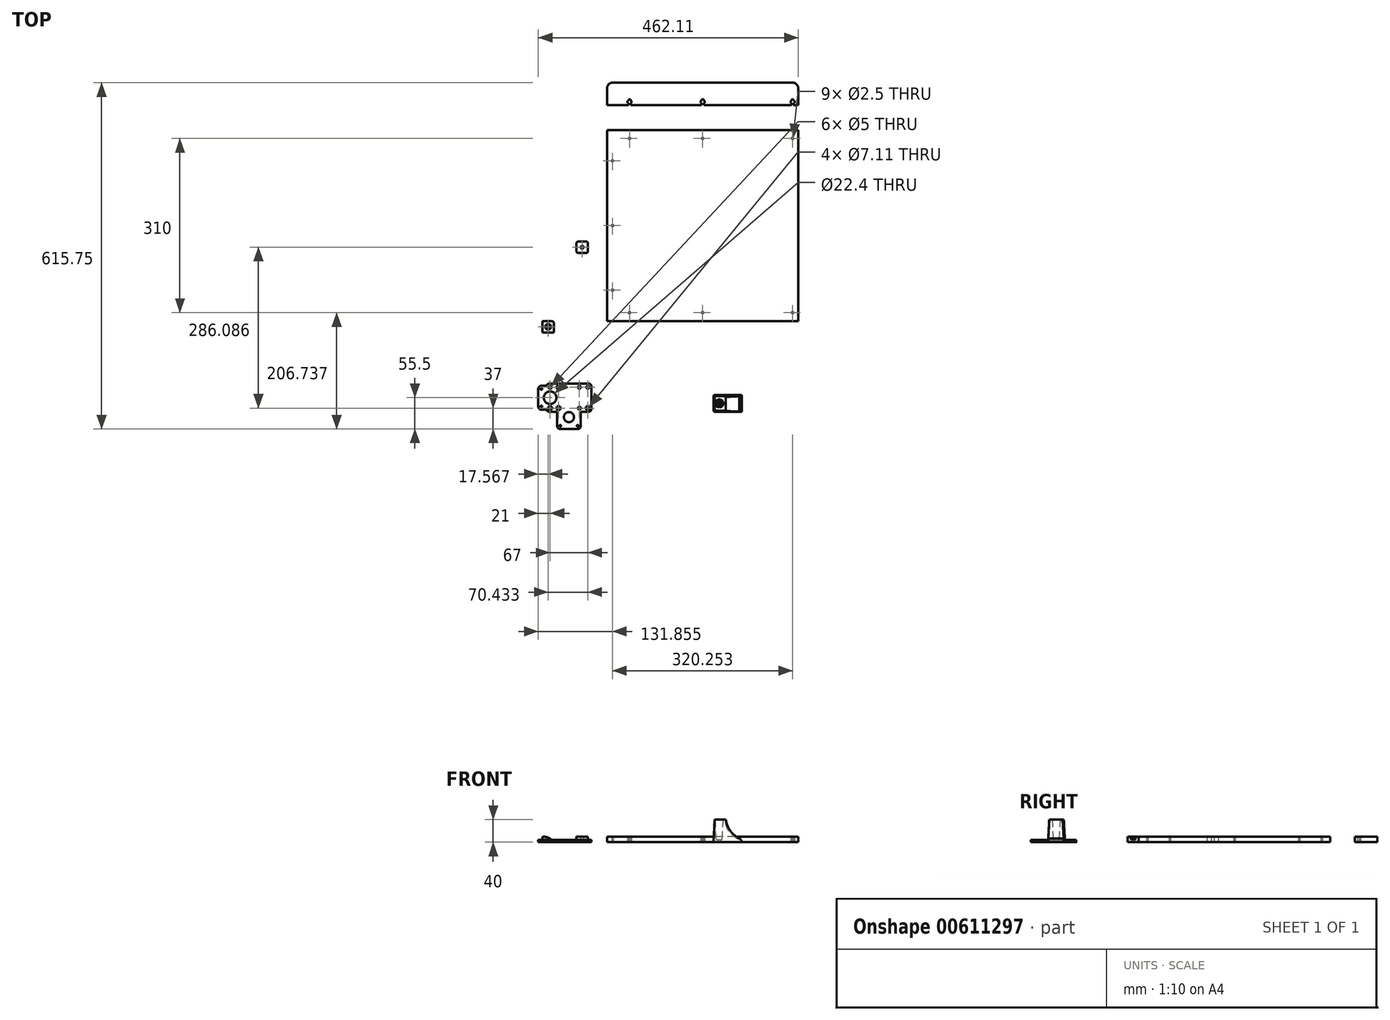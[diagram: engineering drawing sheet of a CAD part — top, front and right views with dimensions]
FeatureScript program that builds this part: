
annotation { "Feature Type Name" : "Feature", "Feature Type Description" : "" }
export const myFeature = defineFeature(function(context is Context, id is Id, definition is map)
    precondition{}
    {
        {
            var Q0;
            Q0=qCreatedBy(makeId("Top.planeOp"),FACE);
            var sketch = newSketch(context, id + "F0", { "sketchPlane" : qUnion([Q0])});
            skLineSegment(sketch, "E0.left", {"start": v(-18.5, 18.5) * mm, "end": v(-18.5, -18.5) * mm, "construction": true});
            skLineSegment(sketch, "E0.right", {"start": v(18.5, 18.5) * mm, "end": v(18.5, -18.5) * mm, "construction": true});
            skCircle(sketch, "E1", {"center": v(-18.5, 18.5) * mm, "radius": 3.56 * mm});
            skCircle(sketch, "E2", {"center": v(18.5, 18.5) * mm, "radius": 2.5 * mm});
            skCircle(sketch, "E3", {"center": v(18.5, -18.5) * mm, "radius": 2.5 * mm});
            skCircle(sketch, "E4", {"center": v(-18.5, -18.5) * mm, "radius": 3.56 * mm});
            skLineSegment(sketch, "E5.bottom", {"start": v(-35, 25) * mm, "end": v(35, 25) * mm});
            skLineSegment(sketch, "E5.top", {"start": v(-35, -25) * mm, "end": v(0.1, -25) * mm});
            skLineSegment(sketch, "E5.right", {"start": v(40, 20) * mm, "end": v(40, -20) * mm});
            skPoint(sketch, "E6.visualSharp", {"position": v(-40, 25) * mm});
            skArc(sketch, "E6.filletArc", {"start": v(-35, 25) * mm, "mid": v(-38.54, 23.54) * mm, "end": v(-40, 20) * mm});
            skPoint(sketch, "E7.visualSharp", {"position": v(40, 25) * mm});
            skArc(sketch, "E7.filletArc", {"start": v(40, 20) * mm, "mid": v(38.54, 23.54) * mm, "end": v(35, 25) * mm});
            skPoint(sketch, "E8.visualSharp", {"position": v(40, -25) * mm});
            skArc(sketch, "E8.filletArc", {"start": v(35, -25) * mm, "mid": v(38.54, -23.54) * mm, "end": v(40, -20) * mm});
            skPoint(sketch, "E9.visualSharp", {"position": v(-40, -25) * mm});
            skArc(sketch, "E9.filletArc", {"start": v(-40, -20) * mm, "mid": v(-38.54, -23.54) * mm, "end": v(-35, -25) * mm});
            skLineSegment(sketch, "E10.bottom", {"start": v(407.6, 136.24) * mm, "end": v(67.6, 136.24) * mm});
            skLineSegment(sketch, "E10.top", {"start": v(407.6, 476.24) * mm, "end": v(67.6, 476.24) * mm});
            skLineSegment(sketch, "E10.left", {"start": v(407.6, 136.24) * mm, "end": v(407.6, 476.24) * mm});
            skLineSegment(sketch, "E10.right", {"start": v(67.6, 136.24) * mm, "end": v(67.6, 476.24) * mm});
            skCircle(sketch, "E11", {"center": v(-33.5, -18.5) * mm, "radius": 3.56 * mm});
            skCircle(sketch, "E12", {"center": v(33.5, -18.5) * mm, "radius": 3.56 * mm});
            skCircle(sketch, "E13", {"center": v(-33.5, 18.5) * mm, "radius": 2.5 * mm});
            skCircle(sketch, "E14", {"center": v(33.5, 18.5) * mm, "radius": 2.5 * mm});
            skPoint(sketch, "E15.middle.positionSnap0", {"position": v(-40, 0) * mm});
            skPoint(sketch, "E15.centerSnap0", {"position": v(-40, 0) * mm});
            skLineSegment(sketch, "E16.top", {"start": v(-15.5, -50) * mm, "end": v(15.5, -50) * mm, "construction": true});
            skLineSegment(sketch, "E16.left", {"start": v(-15.5, -19) * mm, "end": v(-15.5, -50) * mm, "construction": true});
            skLineSegment(sketch, "E16.right", {"start": v(15.5, -19) * mm, "end": v(15.5, -50) * mm, "construction": true});
            skPoint(sketch, "E16.middle", {"position": v(0, -34.5) * mm});
            skLineSegment(sketch, "E17.bottom", {"start": v(21, -13.5) * mm, "end": v(18.5, -13.5) * mm});
            skLineSegment(sketch, "E17.top", {"start": v(16, -55.5) * mm, "end": v(-16, -55.5) * mm});
            skLineSegment(sketch, "E17.left", {"start": v(21, -25) * mm, "end": v(21, -50.5) * mm});
            skLineSegment(sketch, "E17.right", {"start": v(-21, -15.97) * mm, "end": v(-21, -21.03) * mm});
            skCircle(sketch, "E18", {"center": v(0, -34.5) * mm, "radius": 9 * mm});
            skCircle(sketch, "E19", {"center": v(-15.5, -50) * mm, "radius": 1.5 * mm});
            skCircle(sketch, "E20", {"center": v(15.5, -50) * mm, "radius": 1.5 * mm});
            skPoint(sketch, "E21.visualSharp", {"position": v(-21, -55.5) * mm});
            skArc(sketch, "E21.filletArc", {"start": v(-21, -50.5) * mm, "mid": v(-19.54, -54.04) * mm, "end": v(-16, -55.5) * mm});
            skPoint(sketch, "E22.visualSharp", {"position": v(21, -55.5) * mm});
            skArc(sketch, "E22.filletArc", {"start": v(16, -55.5) * mm, "mid": v(19.54, -54.04) * mm, "end": v(21, -50.5) * mm});
            skLineSegment(sketch, "E23.bottom", {"start": v(-49, 15.5) * mm, "end": v(-47.5, 15.5) * mm, "construction": true});
            skLineSegment(sketch, "E23.top", {"start": v(-49, -15.5) * mm, "end": v(-18, -15.5) * mm, "construction": true});
            skLineSegment(sketch, "E23.left", {"start": v(-49, 15.5) * mm, "end": v(-49, -15.5) * mm, "construction": true});
            skLineSegment(sketch, "E23.right", {"start": v(-18, 15.5) * mm, "end": v(-18, -15.5) * mm, "construction": true});
            skCircle(sketch, "E24", {"center": v(-33.5, 0) * mm, "radius": 11.2 * mm});
            skCircle(sketch, "E25", {"center": v(-49, -15.5) * mm, "radius": 1.5 * mm});
            skCircle(sketch, "E26", {"center": v(-49, 15.5) * mm, "radius": 1.5 * mm});
            skPoint(sketch, "E27.visualSharp", {"position": v(-13.5, -20) * mm});
            skLineSegment(sketch, "E28.trimOffspring", {"start": v(-40, 15.5) * mm, "end": v(-18, 15.5) * mm, "construction": true});
            skLineSegment(sketch, "E29.trimOffspring", {"start": v(-21, -25) * mm, "end": v(-21, -50.5) * mm});
            skLineSegment(sketch, "E30.trimOffspring", {"start": v(15.5, -25) * mm, "end": v(35, -25) * mm});
            skLineSegment(sketch, "E31.bottom", {"start": v(-49.5, 21) * mm, "end": v(-39.9, 21) * mm});
            skLineSegment(sketch, "E31.top", {"start": v(-49.5, -21) * mm, "end": v(-39.9, -21) * mm});
            skLineSegment(sketch, "E31.left", {"start": v(-54.5, 16) * mm, "end": v(-54.5, -16) * mm});
            skLineSegment(sketch, "E31.right", {"start": v(-12.5, 21) * mm, "end": v(-12.5, 18.5) * mm});
            skLineSegment(sketch, "E32.trimOffspring", {"start": v(-12.5, -13.5) * mm, "end": v(-12.5, -21) * mm});
            skPoint(sketch, "E33.visualSharp", {"position": v(-54.5, -21) * mm});
            skArc(sketch, "E33.filletArc", {"start": v(-54.5, -16) * mm, "mid": v(-53.04, -19.54) * mm, "end": v(-49.5, -21) * mm});
            skPoint(sketch, "E34.visualSharp", {"position": v(-54.5, 21) * mm});
            skArc(sketch, "E34.filletArc", {"start": v(-49.5, 21) * mm, "mid": v(-53.04, 19.54) * mm, "end": v(-54.5, 16) * mm});
            skLineSegment(sketch, "E35.right", {"start": v(257.17, 4.9) * mm, "end": v(257.17, -25.1) * mm});
            skCircle(sketch, "E36", {"center": v(267.17, -10.1) * mm, "radius": 5 * mm});
            skCircle(sketch, "E37", {"center": v(267.17, -10.1) * mm, "radius": 2 * mm});
            skLineSegment(sketch, "E38.right", {"start": v(307.17, -25.1) * mm, "end": v(307.17, 4.9) * mm});
            skLineSegment(sketch, "E39.bottom", {"start": v(-46.93, 136.1) * mm, "end": v(-26.93, 136.1) * mm});
            skLineSegment(sketch, "E39.top", {"start": v(-46.93, 116.1) * mm, "end": v(-26.93, 116.1) * mm});
            skLineSegment(sketch, "E39.left", {"start": v(-46.93, 136.1) * mm, "end": v(-46.93, 116.1) * mm});
            skLineSegment(sketch, "E39.right", {"start": v(-26.93, 136.1) * mm, "end": v(-26.93, 116.1) * mm});
            skCircle(sketch, "E40", {"center": v(-36.93, 126.1) * mm, "radius": 2.5 * mm});
            skPoint(sketch, "E40.centerSnap0", {"position": v(-36.93, 136.1) * mm});
            skPoint(sketch, "E40.centerSnap1", {"position": v(-46.93, 126.1) * mm});
            skCircle(sketch, "E41", {"center": v(-36.93, 126.1) * mm, "radius": 5 * mm});
            skLineSegment(sketch, "E42", {"start": v(77.6, 136.24) * mm, "end": v(77.6, 476.24) * mm, "construction": true});
            skPoint(sketch, "E43", {"position": v(77.6, 191.24) * mm});
            skPoint(sketch, "E44", {"position": v(77.6, 306.24) * mm});
            skPoint(sketch, "E45", {"position": v(77.36, 421.24) * mm});
            skLineSegment(sketch, "E46", {"start": v(257.17, -25.1) * mm, "end": v(307.17, -25.1) * mm});
            skLineSegment(sketch, "E47", {"start": v(307.17, 4.9) * mm, "end": v(257.17, 4.9) * mm});
            skLineSegment(sketch, "E48", {"start": v(397.6, 136.24) * mm, "end": v(397.6, 476.24) * mm, "construction": true});
            skPoint(sketch, "E49", {"position": v(397.6, 151.24) * mm});
            skPoint(sketch, "E50", {"position": v(397.6, 461.24) * mm});
            skLineSegment(sketch, "E51.bottom", {"start": v(67.6, 520.25) * mm, "end": v(407.6, 520.25) * mm});
            skLineSegment(sketch, "E51.top", {"start": v(77.6, 560.25) * mm, "end": v(397.6, 560.25) * mm});
            skLineSegment(sketch, "E51.left", {"start": v(67.6, 520.25) * mm, "end": v(67.6, 550.25) * mm});
            skLineSegment(sketch, "E51.right", {"start": v(407.6, 520.25) * mm, "end": v(407.6, 550.25) * mm});
            skLineSegment(sketch, "E52", {"start": v(77.6, 151.24) * mm, "end": v(397.6, 151.24) * mm, "construction": true});
            skLineSegment(sketch, "E53", {"start": v(77.6, 461.24) * mm, "end": v(397.6, 461.24) * mm, "construction": true});
            skPoint(sketch, "E54", {"position": v(237.6, 461.24) * mm});
            skPoint(sketch, "E55", {"position": v(237.6, 151.24) * mm});
            skPoint(sketch, "E56", {"position": v(77.6, 520.25) * mm});
            skPoint(sketch, "E57", {"position": v(237.6, 520.25) * mm});
            skPoint(sketch, "E58", {"position": v(397.6, 520.25) * mm});
            skLineSegment(sketch, "E59.bottom", {"start": v(395.6, 530.25) * mm, "end": v(399.6, 530.25) * mm});
            skLineSegment(sketch, "E59.top", {"start": v(395.6, 510.25) * mm, "end": v(399.6, 510.25) * mm});
            skLineSegment(sketch, "E59.left", {"start": v(395.6, 530.25) * mm, "end": v(395.6, 510.25) * mm});
            skLineSegment(sketch, "E59.right", {"start": v(399.6, 530.25) * mm, "end": v(399.6, 510.25) * mm});
            skLineSegment(sketch, "E60.bottom", {"start": v(235.6, 530.25) * mm, "end": v(239.6, 530.25) * mm});
            skLineSegment(sketch, "E60.top", {"start": v(235.6, 510.25) * mm, "end": v(239.6, 510.25) * mm});
            skLineSegment(sketch, "E60.left", {"start": v(235.6, 530.25) * mm, "end": v(235.6, 510.25) * mm});
            skLineSegment(sketch, "E60.right", {"start": v(239.6, 530.25) * mm, "end": v(239.6, 510.25) * mm});
            skLineSegment(sketch, "E61.bottom", {"start": v(109.6, 530.25) * mm, "end": v(105.6, 530.25) * mm});
            skLineSegment(sketch, "E61.top", {"start": v(109.6, 510.25) * mm, "end": v(105.6, 510.25) * mm});
            skLineSegment(sketch, "E61.left", {"start": v(109.6, 530.25) * mm, "end": v(109.6, 510.25) * mm});
            skLineSegment(sketch, "E61.right", {"start": v(105.6, 530.25) * mm, "end": v(105.6, 510.25) * mm});
            skPoint(sketch, "E61.middle", {"position": v(107.6, 520.25) * mm});
            skLineSegment(sketch, "E62.bottom", {"start": v(394.1, 527.72) * mm, "end": v(401.1, 527.72) * mm});
            skLineSegment(sketch, "E62.top", {"start": v(394.1, 524.42) * mm, "end": v(401.1, 524.42) * mm});
            skLineSegment(sketch, "E62.left", {"start": v(394.1, 527.72) * mm, "end": v(394.1, 524.42) * mm});
            skLineSegment(sketch, "E62.right", {"start": v(401.1, 527.72) * mm, "end": v(401.1, 524.42) * mm});
            skPoint(sketch, "E62.middle", {"position": v(397.6, 526.07) * mm});
            skLineSegment(sketch, "E63.bottom", {"start": v(241.1, 527.72) * mm, "end": v(234.1, 527.72) * mm});
            skLineSegment(sketch, "E63.top", {"start": v(241.1, 524.42) * mm, "end": v(234.1, 524.42) * mm});
            skLineSegment(sketch, "E63.left", {"start": v(241.1, 527.72) * mm, "end": v(241.1, 524.42) * mm});
            skLineSegment(sketch, "E63.right", {"start": v(234.1, 527.72) * mm, "end": v(234.1, 524.42) * mm});
            skPoint(sketch, "E63.middle", {"position": v(237.6, 526.07) * mm});
            skPoint(sketch, "E64.visualSharp", {"position": v(67.6, 560.25) * mm});
            skArc(sketch, "E64.filletArc", {"start": v(77.6, 560.25) * mm, "mid": v(70.54, 557.32) * mm, "end": v(67.6, 550.25) * mm});
            skPoint(sketch, "E65.visualSharp", {"position": v(407.6, 560.25) * mm});
            skArc(sketch, "E65.filletArc", {"start": v(407.6, 550.25) * mm, "mid": v(404.68, 557.32) * mm, "end": v(397.6, 560.25) * mm});
            skLineSegment(sketch, "E66.bottom", {"start": v(16, 277.59) * mm, "end": v(31, 277.59) * mm});
            skLineSegment(sketch, "E66.top", {"start": v(16, 257.59) * mm, "end": v(31, 257.59) * mm});
            skLineSegment(sketch, "E66.left", {"start": v(13.5, 275.09) * mm, "end": v(13.5, 260.09) * mm});
            skLineSegment(sketch, "E66.right", {"start": v(33.5, 275.09) * mm, "end": v(33.5, 260.09) * mm});
            skPoint(sketch, "E66.middle", {"position": v(23.5, 267.59) * mm});
            skPoint(sketch, "E67.visualSharp", {"position": v(33.5, 257.59) * mm});
            skArc(sketch, "E67.filletArc", {"start": v(31, 257.59) * mm, "mid": v(32.77, 258.32) * mm, "end": v(33.5, 260.09) * mm});
            skPoint(sketch, "E68.visualSharp", {"position": v(13.5, 257.59) * mm});
            skArc(sketch, "E68.filletArc", {"start": v(13.5, 260.09) * mm, "mid": v(14.23, 258.32) * mm, "end": v(16, 257.59) * mm});
            skPoint(sketch, "E69.visualSharp", {"position": v(33.5, 277.59) * mm});
            skArc(sketch, "E69.filletArc", {"start": v(33.5, 275.09) * mm, "mid": v(32.77, 276.85) * mm, "end": v(31, 277.59) * mm});
            skCircle(sketch, "E70", {"center": v(23.5, 267.59) * mm, "radius": 2.5 * mm});
            skPoint(sketch, "E71.visualSharp", {"position": v(13.5, 277.59) * mm});
            skArc(sketch, "E71.filletArc", {"start": v(16, 277.59) * mm, "mid": v(14.23, 276.85) * mm, "end": v(13.5, 275.09) * mm});
            skPoint(sketch, "E72", {"position": v(107.6, 461.24) * mm});
            skPoint(sketch, "E73", {"position": v(107.6, 151.24) * mm});
            skLineSegment(sketch, "E74.bottom", {"start": v(111.1, 524.42) * mm, "end": v(104.1, 524.42) * mm});
            skLineSegment(sketch, "E74.top", {"start": v(111.1, 527.72) * mm, "end": v(104.1, 527.72) * mm});
            skLineSegment(sketch, "E74.left", {"start": v(111.1, 524.42) * mm, "end": v(111.1, 527.72) * mm});
            skLineSegment(sketch, "E74.right", {"start": v(104.1, 524.42) * mm, "end": v(104.1, 527.72) * mm});
            skPoint(sketch, "E74.middle", {"position": v(107.6, 526.07) * mm});
            skSolve(sketch);
        }
        {
            var Q0;
            Q0=makeQuery(id+"F0.imprint","IMPRINT",FACE,{"disambiguationData":[TD([[makeQuery(id+"F0.imprint","IMPRINT",EDGE,{"derivedFrom":sQuery(id+"F0.wireOp",EDGE,"E1")}),-1.0]])]});
            var Q1;
            Q1=makeQuery(id+"F0.imprint","IMPRINT",FACE,{"disambiguationData":[TD([[makeQuery(id+"F0.imprint","IMPRINT",EDGE,{"derivedFrom":sQuery(id+"F0.wireOp",EDGE,"5QKgwCEY-hStk-wvY1-uHoH-thM2InlFBlLN.top")}),-1.0]])]});
            var Q2;
            Q2=makeQuery(id+"F0.imprint","IMPRINT",FACE,{"disambiguationData":[TD([[makeQuery(id+"F0.imprint","IMPRINT",EDGE,{"derivedFrom":sQuery(id+"F0.wireOp",EDGE,"DSqGHO2r-ZKHx-pAYN-DuYB-4O4wjz5FZ1oX.bottom")}),-1.0]])]});
            var Q3;
            Q3=makeQuery(id+"F0.imprint","IMPRINT",FACE,{"disambiguationData":[TD([[makeQuery(id+"F0.imprint","IMPRINT",EDGE,{"derivedFrom":sQuery(id+"F0.wireOp",EDGE,"HSy17Wos-LkgW-PUzs-iLZR-7mMcprWT0IVK.bottom")}),1.0]])]});
            var Q4;
            Q4=makeQuery(id+"F0.imprint","IMPRINT",FACE,{"disambiguationData":[TD([[makeQuery(id+"F0.imprint","IMPRINT",EDGE,{"derivedFrom":sQuery(id+"F0.wireOp",EDGE,"0c0f4aba-d832-4a81-b14c-29bbfecc0367.right")}),1.0]])]});
            extrude(context, id + "F1", {"entities" : qUnion([Q0, Q1, Q2, Q3, Q4]), "depth" : 4 * mm});
        }
        {
            var Q0;
            Q0=makeQuery(id+"F0.imprint","IMPRINT",FACE,{"disambiguationData":[TD([[makeQuery(id+"F0.imprint","IMPRINT",EDGE,{"derivedFrom":sQuery(id+"F0.wireOp",EDGE,"E10.bottom")}),-1.0]])]});
            var Q1;
            Q1=makeQuery(id+"F0.imprint","IMPRINT",FACE,{"disambiguationData":[TD([[makeQuery(id+"F0.imprint","IMPRINT",EDGE,{"derivedFrom":sQuery(id+"F0.wireOp",EDGE,"E66.bottom")}),-1.0]])]});
            extrude(context, id + "F2", {"entities" : qUnion([Q0, Q1]), "depth" : 10 * mm});
        }
        {
            var Q0;
            Q0=makeQuery(id+"F0.imprint","IMPRINT",FACE,{"disambiguationData":[TD([[makeQuery(id+"F0.imprint","IMPRINT",EDGE,{"derivedFrom":sQuery(id+"F0.wireOp",EDGE,"E35.bottom")}),1.0]])]});
            var Q1;
            Q1=makeQuery(id+"F0.imprint","IMPRINT",FACE,{"disambiguationData":[TD([[makeQuery(id+"F0.imprint","IMPRINT",EDGE,{"derivedFrom":sQuery(id+"F0.wireOp",EDGE,"E35.right")}),1.0]])]});
            extrude(context, id + "F3", {"entities" : qUnion([Q0, Q1]), "depth" : 40 * mm, "hasDraft" : true, "draftAngle" : 3 * degree, "draftPullDirection" : true});
        }
        {
            var Q0;
            Q0=makeQuery(id+"F0.imprint","IMPRINT",FACE,{"disambiguationData":[TD([[makeQuery(id+"F0.imprint","IMPRINT",EDGE,{"derivedFrom":sQuery(id+"F0.wireOp",EDGE,"E36")}),1.0]])]});
            extrude(context, id + "F4", {"entities" : qUnion([Q0]), "operationType" : NewBodyOperationType.ADD, "depth" : 4 * mm, "hasDraft" : true, "draftAngle" : 3 * degree});
        }
        {
            var Q0;
            Q0=qCreatedBy(makeId("Front.planeOp"),FACE);
            var sketch = newSketch(context, id + "F5", { "sketchPlane" : qUnion([Q0])});
            skArc(sketch, "E75", {"start": v(307.17, 0) * mm, "mid": v(305.91, 3.8) * mm, "end": v(302.9, 6.41) * mm});
            skArc(sketch, "E76", {"start": v(278.53, 41.5) * mm, "mid": v(286.23, 20.84) * mm, "end": v(302.9, 6.41) * mm});
            skLineSegment(sketch, "E77", {"start": v(278.53, 41.5) * mm, "end": v(307.17, 41.5) * mm});
            skLineSegment(sketch, "E78", {"start": v(307.17, 41.5) * mm, "end": v(307.17, 0) * mm});
            skSolve(sketch);
        }
        {
            var Q0;
            {var subQ0=sQuery(id+"F5.wireOp",EDGE,"E75");Q0=makeQuery(id+"F5.imprint","IMPRINT",FACE,{"disambiguationData":[TD([[makeQuery(id+"F5.imprint","IMPRINT",EDGE,{"derivedFrom":subQ0}),-1.0]])]});}
            var Q1;
            {var subQ0=sQuery(id+"F5.wireOp",EDGE,"E77");Q1=makeQuery(id+"F5.imprint","IMPRINT",FACE,{"disambiguationData":[TD([[makeQuery(id+"F5.imprint","IMPRINT",EDGE,{"derivedFrom":subQ0}),-1.0]])]});}
            extrude(context, id + "F6", {"entities" : qUnion([Q0, Q1]), "operationType" : NewBodyOperationType.REMOVE, "depth" : 39.1 * mm, "hasSecondDirection" : true, "secondDirectionOppositeDirection" : true, "secondDirectionDepth" : 25 * mm});
        }
        {
            var Q0;
            Q0=makeQuery(id+"F3.opExtrude","SWEPT_EDGE",EDGE,{"disambiguationData":[OSD([sQuery(id+"F0.wireOp",EDGE,"E35.right"),sQuery(id+"F0.wireOp",EDGE,"E47")])]});
            var Q1;
            Q1=makeQuery(id+"F3.opExtrude","SWEPT_EDGE",EDGE,{"disambiguationData":[OSD([sQuery(id+"F0.wireOp",EDGE,"E35.right"),sQuery(id+"F0.wireOp",EDGE,"E46")])]});
            var Q2;
            Q2=makeQuery(id+"F3.opExtrude","SWEPT_EDGE",EDGE,{"disambiguationData":[OSD([sQuery(id+"F0.wireOp",EDGE,"E35.right"),sQuery(id+"F0.wireOp",EDGE,"E47")])]});
            var Q3;
            Q3=makeQuery(id+"F6.boolean.opBoolean","COPY",EDGE,{"derivedFrom":makeQuery(id+"F6.opExtrude","CAP_EDGE",EDGE,{"disambiguationData":[OSD([sQuery(id+"F5.wireOp",EDGE,"E75")])],"isStart":true})});
            var Q4;
            {var subQ0=sQuery(id+"F0.wireOp",EDGE,"E36");Q4=makeQuery(id+"F6.boolean.opBoolean","INTERSECT",EDGE,{"derivedFrom":[makeQuery(id+"F4.boolean.opBoolean","MERGE",FACE,{"derivedFrom":[makeQuery(id+"F3.opExtrude","CAP_FACE",FACE,{"disambiguationData":[OSD([sQuery(id+"F0.wireOp",EDGE,"E35.right"),subQ0,sQuery(id+"F0.wireOp",EDGE,"E38.right"),sQuery(id+"F0.wireOp",EDGE,"E46"),sQuery(id+"F0.wireOp",EDGE,"E47")])],"isStart":true}),makeQuery(id+"F4.opExtrude","CAP_FACE",FACE,{"disambiguationData":[OSD([subQ0,sQuery(id+"F0.wireOp",EDGE,"E37")])],"isStart":true})]}),makeQuery(id+"F6.opExtrude","SWEPT_FACE",FACE,{"disambiguationData":[OSD([sQuery(id+"F5.wireOp",EDGE,"E75")])]})]});}
            var Q5;
            Q5=makeQuery(id+"F6.boolean.opBoolean","INTERSECT",EDGE,{"derivedFrom":[makeQuery(id+"F3.opExtrude","SWEPT_FACE",FACE,{"disambiguationData":[OSD([sQuery(id+"F0.wireOp",EDGE,"E47")])]}),makeQuery(id+"F6.opExtrude","SWEPT_FACE",FACE,{"disambiguationData":[OSD([sQuery(id+"F5.wireOp",EDGE,"E75")])]})]});
            fillet(context, id + "F7", {"entities" : qUnion([Q0, Q1, Q2, Q3, Q4, Q5]), "radius" : 2 * mm, "tangentPropagation" : true, "allowEdgeOverflow" : false});
        }
        {
            var Q0;
            Q0=makeQuery(id+"F0.imprint","IMPRINT",FACE,{"disambiguationData":[TD([[makeQuery(id+"F0.imprint","IMPRINT",EDGE,{"derivedFrom":sQuery(id+"F0.wireOp",EDGE,"E39.bottom")}),-1.0]])]});
            extrude(context, id + "F8", {"entities" : qUnion([Q0]), "depth" : 10 * mm});
        }
        {
            var Q0;
            Q0=makeQuery(id+"F0.imprint","IMPRINT",FACE,{"disambiguationData":[TD([[makeQuery(id+"F0.imprint","IMPRINT",EDGE,{"derivedFrom":sQuery(id+"F0.wireOp",EDGE,"E40")}),-1.0]])]});
            extrude(context, id + "F9", {"entities" : qUnion([Q0]), "operationType" : NewBodyOperationType.ADD, "depth" : 4 * mm});
        }
        {
            var Q0;
            Q0=makeQuery(id+"F8.opExtrude","SWEPT_FACE",FACE,{"disambiguationData":[OSD([sQuery(id+"F0.wireOp",EDGE,"E39.top")])]});
            var sketch = newSketch(context, id + "F10", { "sketchPlane" : qUnion([Q0])});
            skArc(sketch, "E79", {"start": v(-26.93, 0) * mm, "mid": v(-35.75, 7.36) * mm, "end": v(-46.93, 10) * mm});
            skSolve(sketch);
        }
        {
            var Q0;
            Q0=makeQuery(id+"F10.imprint","IMPRINT",FACE,{"disambiguationData":[TD([[makeQuery(id+"F10.imprint","IMPRINT",EDGE,{"derivedFrom":sQuery(id+"F10.wireOp",EDGE,"E79")}),-1.0]])]});
            extrude(context, id + "F11", {"entities" : qUnion([Q0]), "operationType" : NewBodyOperationType.REMOVE, "oppositeDirection" : true, "depth" : 25 * mm});
        }
        {
            var Q0;
            Q0=makeQuery(id+"F11.boolean.opBoolean","COPY",EDGE,{"derivedFrom":makeQuery(id+"F11.opExtrude","CAP_EDGE",EDGE,{"disambiguationData":[OSD([sQuery(id+"F10.wireOp",EDGE,"E79")])],"isStart":true})});
            var Q1;
            Q1=makeQuery(id+"F11.boolean.opBoolean","INTERSECT",EDGE,{"derivedFrom":[makeQuery(id+"F8.opExtrude","SWEPT_FACE",FACE,{"disambiguationData":[OSD([sQuery(id+"F0.wireOp",EDGE,"E39.bottom")])]}),makeQuery(id+"F11.opExtrude","SWEPT_FACE",FACE,{"disambiguationData":[OSD([sQuery(id+"F10.wireOp",EDGE,"E79")])]})]});
            fillet(context, id + "F12", {"entities" : qUnion([Q0, Q1]), "radius" : 3 * mm, "tangentPropagation" : true, "allowEdgeOverflow" : false});
        }
        {
            var Q0;
            Q0=sQuery(id+"F0.wireOp",VERTEX,"dd571d82-195f-4a9d-bc1b-d0bfa332f0c7");
            var Q1;
            Q1=sQuery(id+"F0.wireOp",VERTEX,"E43");
            var Q2;
            Q2=sQuery(id+"F0.wireOp",VERTEX,"E44");
            var Q3;
            Q3=sQuery(id+"F0.wireOp",VERTEX,"E45");
            var Q4;
            Q4=sQuery(id+"F0.wireOp",VERTEX,"4b80c046-3122-48b7-a17c-33549950ae94");
            var Q5;
            Q5=sQuery(id+"F0.wireOp",VERTEX,"E49");
            var Q6;
            Q6=sQuery(id+"F0.wireOp",VERTEX,"E50");
            var Q7;
            Q7=sQuery(id+"F0.wireOp",VERTEX,"E54");
            var Q8;
            Q8=sQuery(id+"F0.wireOp",VERTEX,"E55");
            var Q9;
            Q9=sQuery(id+"F0.wireOp",VERTEX,"E72");
            var Q10;
            Q10=sQuery(id+"F0.wireOp",VERTEX,"E73");
            var Q11;
            Q11=makeQuery(id+"F2.opExtrude","SWEPT_BODY",BODY,{"disambiguationData":[OSD([sQuery(id+"F0.wireOp",EDGE,"E10.bottom"),sQuery(id+"F0.wireOp",EDGE,"E10.top"),sQuery(id+"F0.wireOp",EDGE,"E10.left"),sQuery(id+"F0.wireOp",EDGE,"E10.right")])]});
            hole(context, id + "F13", {"style" : HoleStyle.SIMPLE, "endStyle" : HoleEndStyle.BLIND, "oppositeDirection" : true, "holeDiameter" : 2.5 * mm, "holeDepth" : 20 * mm, "tappedDepth" : 12 * mm, "tapClearance" : 3, "locations" : qUnion([Q0, Q1, Q2, Q3, Q4, Q5, Q6, Q7, Q8, Q9, Q10]), "scope" : qUnion([Q11])});
        }
        {
            var Q0;
            Q0=makeQuery(id+"F0.imprint","IMPRINT",FACE,{"disambiguationData":[TD([[makeQuery(id+"F0.imprint","IMPRINT",EDGE,{"derivedFrom":sQuery(id+"F0.wireOp",EDGE,"E51.bottom")}),1.0]])]});
            extrude(context, id + "F14", {"entities" : qUnion([Q0]), "depth" : 10 * mm});
        }
    });
